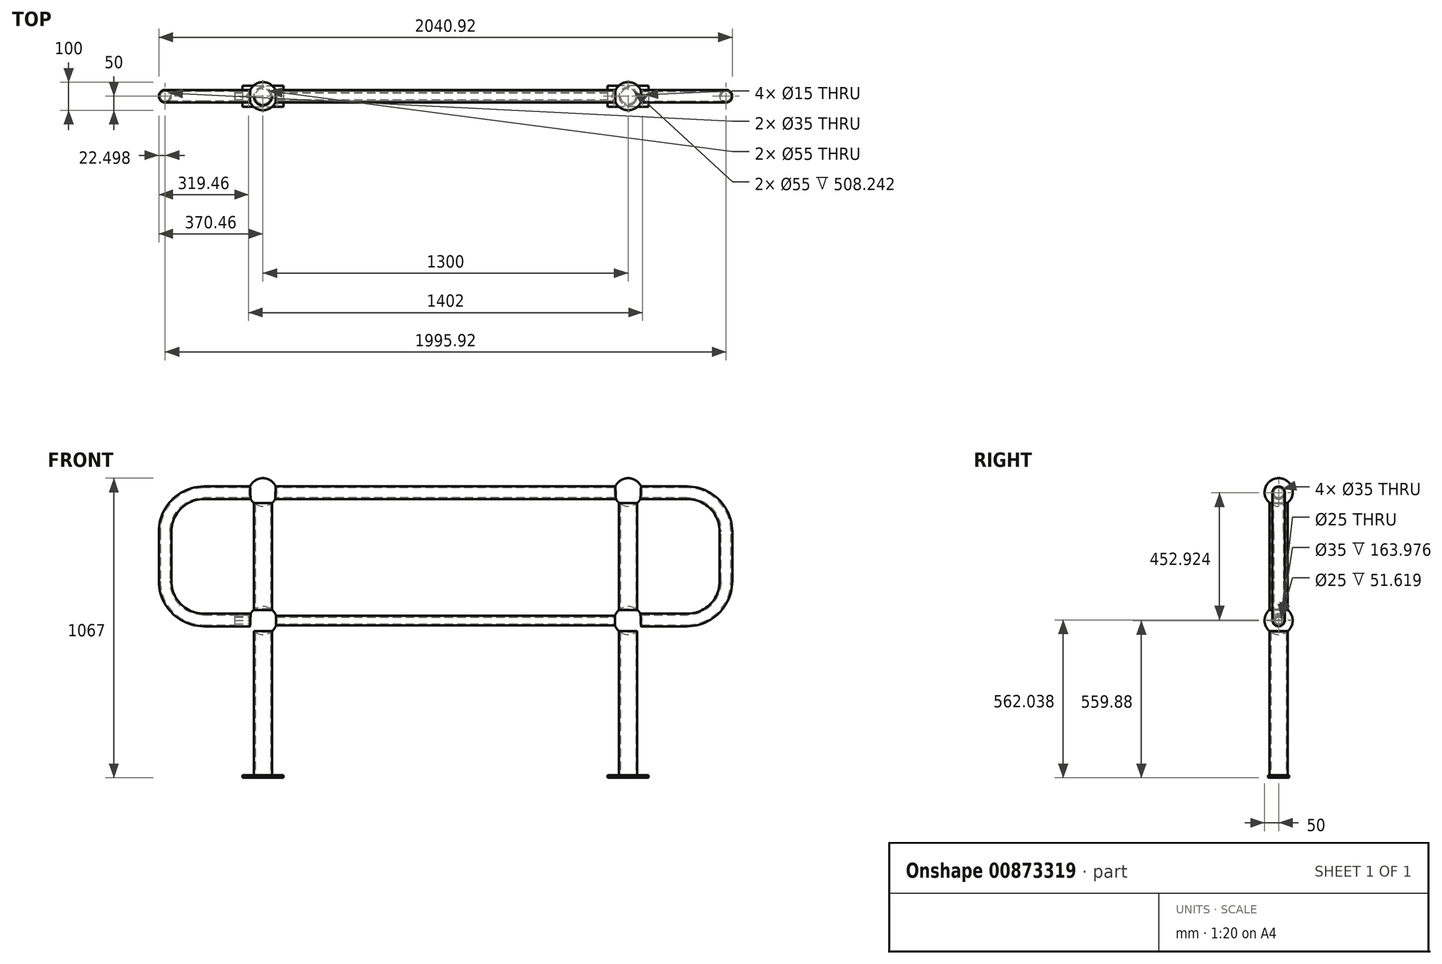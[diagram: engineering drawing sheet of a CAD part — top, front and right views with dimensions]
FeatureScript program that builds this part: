
annotation { "Feature Type Name" : "Feature", "Feature Type Description" : "" }
export const myFeature = defineFeature(function(context is Context, id is Id, definition is map)
    precondition{}
    {
        {
            var Q0;
            Q0=qCreatedBy(makeId("Front.planeOp"),FACE);
            var sketch = newSketch(context, id + "F0", { "sketchPlane" : qUnion([Q0])});
            skLineSegment(sketch, "E0", {"start": v(0, 560) * mm, "end": v(210, 560) * mm});
            skLineSegment(sketch, "E1", {"start": v(0, 0) * mm, "end": v(0, 1017) * mm, "construction": true});
            skLineSegment(sketch, "E2", {"start": v(0, 1017) * mm, "end": v(210, 1017) * mm});
            skArc(sketch, "E3", {"start": v(210, 1017) * mm, "mid": v(309, 976) * mm, "end": v(350, 877) * mm});
            skArc(sketch, "E4", {"start": v(210, 560) * mm, "mid": v(309, 601) * mm, "end": v(350, 700) * mm});
            skLineSegment(sketch, "E5", {"start": v(350, 877) * mm, "end": v(350, 700) * mm});
            skLineSegment(sketch, "E6", {"start": v(0, 0) * mm, "end": v(-650, 0) * mm, "construction": true});
            skLineSegment(sketch, "E7", {"start": v(-650, 0) * mm, "end": v(-650, 150) * mm, "construction": true});
            skLineSegment(sketch, "E8.MirrorCS", {"start": v(-1300, 560) * mm, "end": v(-1510, 560) * mm});
            skArc(sketch, "E9.MirrorCS", {"start": v(-1510, 1017) * mm, "mid": v(-1609, 976) * mm, "end": v(-1650, 877) * mm});
            skLineSegment(sketch, "E10.MirrorCS", {"start": v(-1650, 877) * mm, "end": v(-1650, 700) * mm});
            skLineSegment(sketch, "E11.MirrorCS", {"start": v(-1300, 1017) * mm, "end": v(-1510, 1017) * mm});
            skArc(sketch, "E12.MirrorCS", {"start": v(-1510, 560) * mm, "mid": v(-1609, 601) * mm, "end": v(-1650, 700) * mm});
            skLineSegment(sketch, "E13", {"start": v(-1300, 1017) * mm, "end": v(0, 1017) * mm});
            skSolve(sketch);
        }
        {
            var Q0;
            Q0=qCreatedBy(makeId("Right.planeOp"),FACE);
            var sketch = newSketch(context, id + "F1", { "sketchPlane" : qUnion([Q0])});
            skCircle(sketch, "E14", {"center": v(0, 562.04) * mm, "radius": 22.5 * mm});
            skCircle(sketch, "E15", {"center": v(0, 562.04) * mm, "radius": 17.5 * mm});
            skSolve(sketch);
        }
        {
            var Q0;
            Q0 = qSketchRegion(id + "F1", true);
            var Q1;
            Q1 = qConstructionFilter(qBodyType(qCreatedBy(id + "F0" ,EDGE), BodyType.WIRE), ConstructionObject.NO);
            sweep(context, id + "F2", {"profiles" : qUnion([Q0]), "path" : qUnion([Q1])});
        }
        {
            var Q0;
            Q0=qCreatedBy(makeId("Top.planeOp"),FACE);
            var sketch = newSketch(context, id + "F3", { "sketchPlane" : qUnion([Q0])});
            skCircle(sketch, "E16", {"center": v(0, 0) * mm, "radius": 32.5 * mm});
            skCircle(sketch, "E17", {"center": v(0, 0) * mm, "radius": 27.5 * mm});
            skSolve(sketch);
        }
        {
            var Q0;
            Q0 = qSketchRegion(id + "F3", true);
            extrude(context, id + "F4", {"entities" : qUnion([Q0]), "depth" : 1017 * mm, "offsetDistance" : 25 * mm, "hasSecondDirection" : true, "secondDirectionOppositeDirection" : false, "secondDirectionDepth" : 10 * mm});
        }
        {
            var Q0;
            {var subQ0=sQuery(id+"F3.wireOp",EDGE,"E16");var subQ1=sQuery(id+"F3.wireOp",EDGE,"E17");Q0=makeQuery(id+"F4.boolean.opBoolean","SPLIT",FACE,{"disambiguationData":[TD([makeQuery(id+"F2.opSweep","SWEPT_FACE",FACE,{"disambiguationData":[OSD([sQuery(id+"F0.wireOp",EDGE,"E2"),sQuery(id+"F1.wireOp",EDGE,"E14")])]}),makeQuery(id+"F4.opExtrude","SWEPT_FACE",FACE,{"disambiguationData":[OSD([subQ0])]}),makeQuery(id+"F4.opExtrude","SWEPT_FACE",FACE,{"disambiguationData":[OSD([subQ1])]})]),OD(0.0)],"derivedFrom":makeQuery(id+"F4.opExtrude","CAP_FACE",FACE,{"disambiguationData":[OSD([subQ0,subQ1])],"isStart":false})});}
            var sketch = newSketch(context, id + "F5", { "sketchPlane" : qUnion([Q0])});
            skArc(sketch, "E18", {"start": v(-50, 0) * mm, "mid": v(0, -50) * mm, "end": v(50, 0) * mm});
            skLineSegment(sketch, "E19", {"start": v(-50, 0) * mm, "end": v(50, 0) * mm});
            skSolve(sketch);
        }
        {
            var Q0;
            Q0 = qSketchRegion(id + "F5", true);
            var Q1;
            Q1=sQuery(id+"F5.wireOp",EDGE,"E19");
            revolve(context, id + "F6", {"surfaceOperationType" : NewSurfaceOperationType.NEW, "entities" : qUnion([Q0]), "axis" : qUnion([Q1]), "revolveType" : RevolveType.FULL});
        }
        {
            var Q0;
            Q0=qCreatedBy(makeId("Right.planeOp"),FACE);
            cPlane(context, id + "F7", {"entities" : qUnion([Q0]), "cplaneType" : CPlaneType.OFFSET, "offset" : 650 * mm, "oppositeDirection" : true, "width" : 150 * mm, "height" : 150 * mm});
        }
        {
            var Q0;
            Q0=qCreatedBy(makeId("Top.planeOp"),FACE);
            cPlane(context, id + "F8", {"entities" : qUnion([Q0]), "cplaneType" : CPlaneType.OFFSET, "offset" : 788.5 * mm, "width" : 150 * mm, "height" : 150 * mm});
        }
        {
            var Q0;
            Q0=makeQuery(id+"F6.opRevolve","SWEPT_BODY",BODY,{"disambiguationData":[OSD([sQuery(id+"F5.wireOp",EDGE,"E18"),sQuery(id+"F5.wireOp",EDGE,"5bN2gnFG-oceZ-eyp5-UDG8-bVJ6CN20HeSy")])]});
            var Q1;
            Q1=qCreatedBy(id+"F8.planeOp",FACE);
            mirror(context, id + "F9", {"entities" : qUnion([Q0]), "mirrorPlane" : qUnion([Q1])});
        }
        {
            var Q0;
            Q0=qCreatedBy(makeId("Top.planeOp"),FACE);
            var sketch = newSketch(context, id + "F10", { "sketchPlane" : qUnion([Q0])});
            skLineSegment(sketch, "E20.bottom", {"start": v(73, 37.5) * mm, "end": v(-73, 37.5) * mm});
            skLineSegment(sketch, "E20.top", {"start": v(73, -37.5) * mm, "end": v(-73, -37.5) * mm});
            skLineSegment(sketch, "E20.left", {"start": v(73, 37.5) * mm, "end": v(73, -37.5) * mm});
            skLineSegment(sketch, "E20.right", {"start": v(-73, 37.5) * mm, "end": v(-73, -37.5) * mm});
            skPoint(sketch, "E20.middle", {"position": v(0, 0) * mm});
            skCircle(sketch, "E21", {"center": v(-51, 0) * mm, "radius": 7.5 * mm});
            skCircle(sketch, "E22.MirrorC", {"center": v(51, 0) * mm, "radius": 7.5 * mm});
            skSolve(sketch);
        }
        {
            var Q0;
            Q0 = qSketchRegion(id + "F10", true);
            extrude(context, id + "F11", {"entities" : qUnion([Q0]), "depth" : 10 * mm, "offsetDistance" : 25 * mm});
        }
        {
            var Q0;
            Q0=makeQuery(id+"F4.opExtrude","SWEPT_BODY",BODY,{"disambiguationData":[OSD([sQuery(id+"F3.wireOp",EDGE,"E16"),sQuery(id+"F3.wireOp",EDGE,"E17")])]});
            var Q1;
            Q1=makeQuery(id+"F9.opPattern","COPY",BODY,{"derivedFrom":makeQuery(id+"F6.opRevolve","SWEPT_BODY",BODY,{"disambiguationData":[OSD([sQuery(id+"F5.wireOp",EDGE,"E18"),sQuery(id+"F5.wireOp",EDGE,"E19")])]}),"instanceName":"1"});
            var Q2;
            Q2=makeQuery(id+"F6.opRevolve","SWEPT_BODY",BODY,{"disambiguationData":[OSD([sQuery(id+"F5.wireOp",EDGE,"E18"),sQuery(id+"F5.wireOp",EDGE,"E19")])]});
            var Q3;
            Q3=makeQuery(id+"F11.opExtrude","SWEPT_BODY",BODY,{"disambiguationData":[OSD([sQuery(id+"F10.wireOp",EDGE,"E20.bottom"),sQuery(id+"F10.wireOp",EDGE,"E20.top"),sQuery(id+"F10.wireOp",EDGE,"E20.left"),sQuery(id+"F10.wireOp",EDGE,"E20.right"),sQuery(id+"F10.wireOp",EDGE,"E21"),sQuery(id+"F10.wireOp",EDGE,"E22.MirrorC")])]});
            var Q4;
            Q4=qCreatedBy(id+"F7.planeOp",FACE);
            mirror(context, id + "F12", {"operationType" : NewBodyOperationType.ADD, "entities" : qUnion([Q0, Q1, Q2, Q3]), "mirrorPlane" : qUnion([Q4])});
        }
        {
            var Q0;
            Q0=qCreatedBy(makeId("Right.planeOp"),FACE);
            var sketch = newSketch(context, id + "F13", { "sketchPlane" : qUnion([Q0])});
            skCircle(sketch, "E23", {"center": v(0, 559.88) * mm, "radius": 17.5 * mm});
            skCircle(sketch, "E24", {"center": v(0, 559.88) * mm, "radius": 12.5 * mm});
            skSolve(sketch);
        }
        {
            var Q0;
            Q0 = qSketchRegion(id + "F13", true);
            extrude(context, id + "F14", {"entities" : qUnion([Q0]), "operationType" : NewBodyOperationType.ADD, "oppositeDirection" : true, "depth" : 1400 * mm, "offsetDistance" : 25 * mm});
        }
    });
